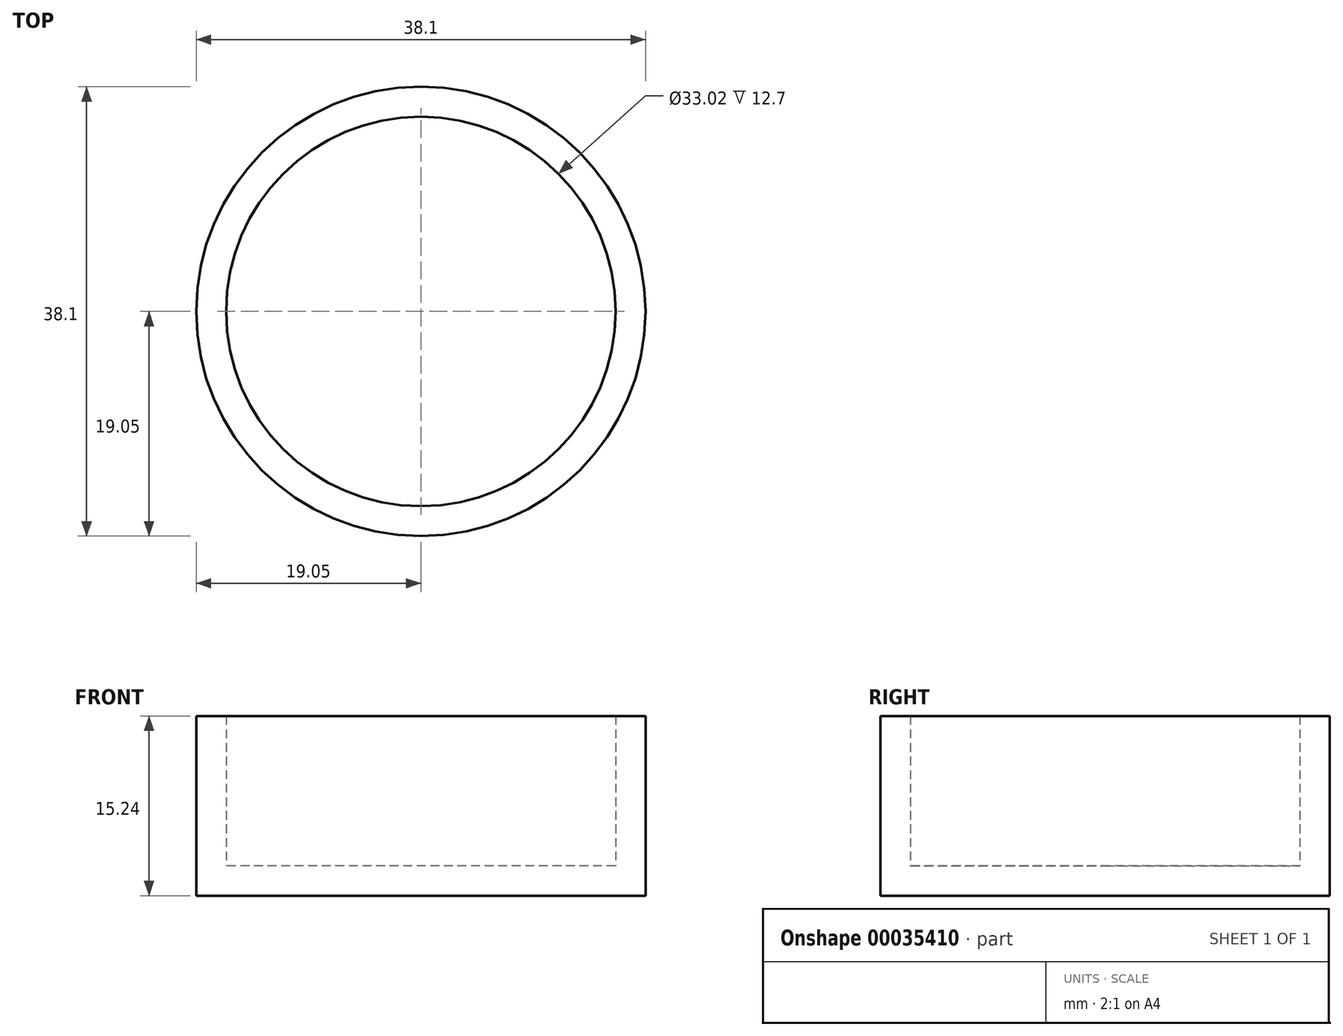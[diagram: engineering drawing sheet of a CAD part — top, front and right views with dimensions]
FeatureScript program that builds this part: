
annotation { "Feature Type Name" : "Feature", "Feature Type Description" : "" }
export const myFeature = defineFeature(function(context is Context, id is Id, definition is map)
    precondition{}
    {
        {
            var Q0;
            Q0=qCreatedBy(makeId("Top.planeOp"),FACE);
            var sketch = newSketch(context, id + "F0", { "sketchPlane" : qUnion([Q0])});
            skCircle(sketch, "E0", {"center": v(0, 0) * mm, "radius": 19.05 * mm});
            skLineSegment(sketch, "E1.bottom", {"start": v(-14.38, 0) * mm, "end": v(3.4, 0) * mm});
            skLineSegment(sketch, "E1.top", {"start": v(-14.38, 108.52) * mm, "end": v(3.4, 108.52) * mm});
            skSolve(sketch);
        }
        {
            var Q0;
            Q0=makeQuery(id+"F0.imprint","IMPRINT",FACE,{"disambiguationData":[TD([[makeQuery(id+"F0.imprint","IMPRINT",EDGE,{"derivedFrom":sQuery(id+"F0.wireOp",EDGE,"E0")}),1.0]])]});
            extrude(context, id + "F1", {"entities" : qUnion([Q0]), "depth" : 15.24 * mm});
        }
        {
            var Q0;
            Q0=makeQuery(id+"F1.opExtrude","CAP_FACE",FACE,{"disambiguationData":[OSD([sQuery(id+"F0.wireOp",EDGE,"E0")])],"isStart":false});
            shell(context, id + "F2", {"entities" : qUnion([Q0]), "thickness" : 2.54 * mm});
        }
    });
